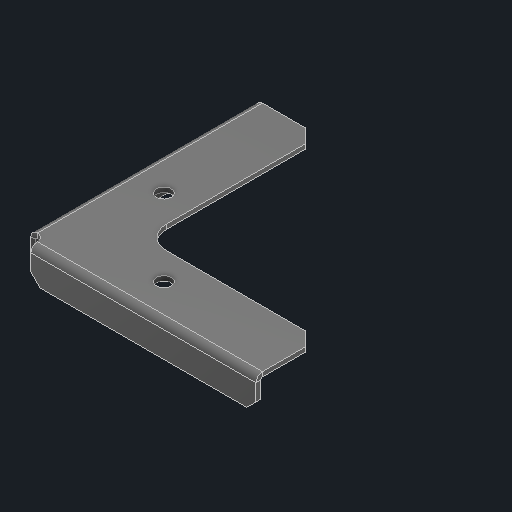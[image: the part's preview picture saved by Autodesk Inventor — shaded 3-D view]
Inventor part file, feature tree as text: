
AUTODESK INVENTOR PART (.ipt)
format: ipt  version: 2024 (Build 280153000, 153)  size: 114,176 bytes
history: native  units: in
note: dims shown in document units (in); Inventor stores cm internally (conversion verified against a paired STEP export)
features: fillet x1
ambient origin geometry x8: Origin, YZ Plane, XZ Plane, XY Plane, X Axis, Y Axis, Z Axis, Center Point
bodies: Solid1 (feature_tree)
feature tree (1):
  fillet  "Fillet1"  [1 undecoded]
note: 1 required parameter value undecoded (feature->parameter linkage not recoverable at this tier; creation-order binding heuristic only, values carry confidence <= 0.55)
